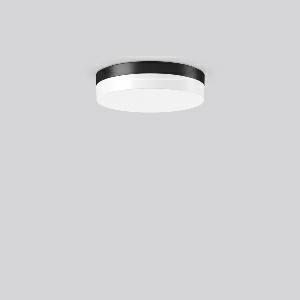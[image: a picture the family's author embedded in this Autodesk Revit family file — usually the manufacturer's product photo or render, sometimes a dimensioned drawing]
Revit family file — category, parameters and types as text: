
# Revit family: flat_slim_round_312630_0031_1_19_b00e
name_source: partatom
category: Lighting Fixtures
units: mm (PartAtom-declared; Revit-internal decimal feet)

## family parameters
Cut with Voids When Loaded = No
Host = Face
Light Source = No
Part Type = Normal
Room Calculation Point = No
Round Connector Dimension = Use Diameter
Shared = No

## types (1)
- MultiLumen 1 830 (1 x LED Modul 830, 1450 lm, 3000)
    Apparent Load = 11 VA
    CIE Flux Codes = 38 68 88 84 100
    Color Rendering = 80
    Color Temperature = 3000
    Default Elevation = 1800 mm
    Height = 70 mm
    Lamp = 1 x LED Modul 830
    Lamp Light Flux = 1450 lm
    Lamp count = 1
    Length = 300 mm
    Lifetime = 50000 h
    Luminous efficacy = 132 lm/W
    Manufacturer = RZB
    ModVariant = No
    Model = 312630.0031.1.19
    Mounting Place = Ceiling
    Mounting Type = Surface mounted
    Number of Poles = 1
    OnlyDefault = Yes
    Power Factor = 1
    Product Name = FLAT SLIM round
    Product group = Surface mounted ceiling and wall luminaires
    ProductGroupID = 305
    Protection Class = Protection class I
    Protection Degree = Degree of protection
    RLX_Detail_Level = 1
    RLX_Emergency_Light_Flux = 0 lm
    RLX_Emergency_Type = 0
    RLX_Emergency_Type_DB = No
    RlxData = <blob elided: 18025 chars, md5=8a1ab7b3>
    Socket = socket
    Standby Power = 0 W
    System Light Flux = 1450 lm
    System Power = 11 W
    Type Comments = MultiLumen 1 830
    Type Image = 312629.0031.jpg
    URL = http://relux.com
    VarID = multilumen_1_830
    Voltage = 0 V
    Weight = 0.00 kg
    Width = 0 mm  [stored 0 ft]

note: [stored X ft] marks values corroborated as IEEE doubles in the binary element streams (Revit-internal decimal feet)

## geometry (parser evidence)
native form markers: Blend x4, Sweep x12
no freeform markers — native parametric forms only
